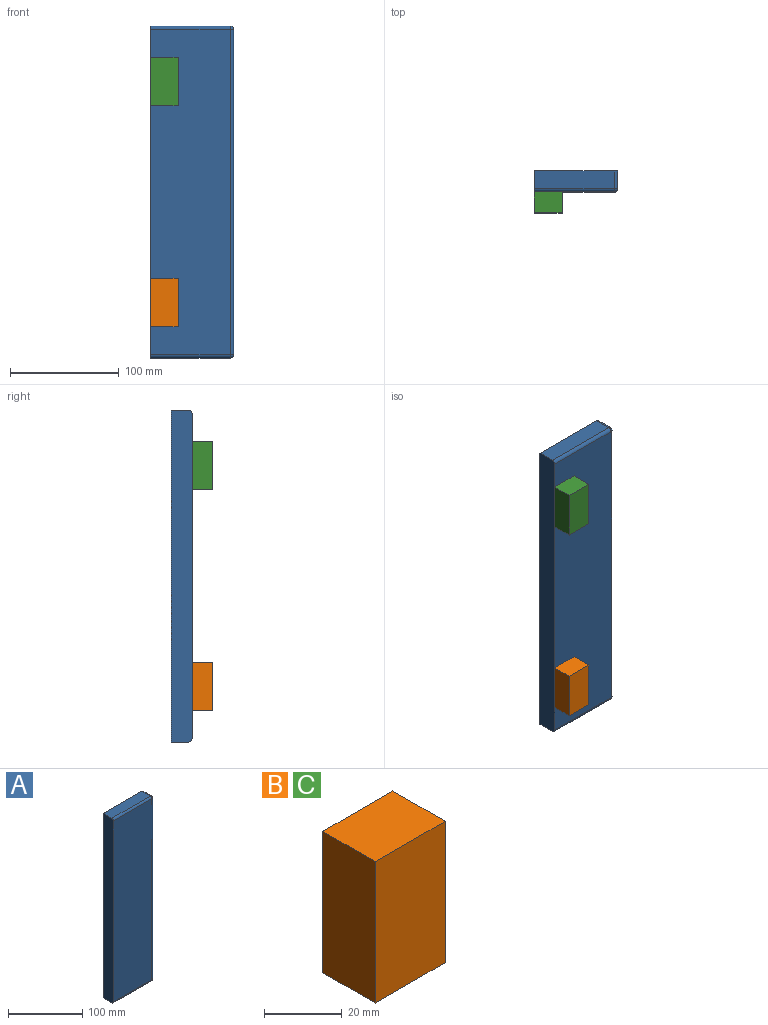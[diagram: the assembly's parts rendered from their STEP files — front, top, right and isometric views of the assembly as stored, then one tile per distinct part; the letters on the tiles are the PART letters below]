
ASSEMBLY  parts=3 mates=2
PART A: 13 faces, bbox 76.2x19.1x304.8 mm
  f0: plane 304.8x19.05mm, normal (-1,0,0), area 5802.6mm2, adj f1,f3,f4,f5,f6,f9
  f1: plane 73.2x16.05mm, normal (0,0,-1), area 1174.9mm2, adj f0,f5,f9,f12
  f2: plane 298.8x16.05mm, normal (1,0,0), area 4795.7mm2, adj f5,f7,f10,f12
  f3: plane 73.2x16.05mm, normal (0,0,1), area 1174.9mm2, adj f0,f5,f6,f7
  f4: plane 298.8x73.2mm, normal (0,-1,0), area 21872.2mm2, adj f0,f6,f9,f10
  f5: plane 304.8x76.2mm, normal (0,1,0), area 23221.9mm2, adj f0,f1,f2,f3,f7,f12
  f6: cylinder r=3mm len=73.2mm, axis (1,0,0), area 344.9mm2, adj f0,f3,f4,f8
  f7: cylinder r=3mm len=16.05mm, axis (0,-1,0), area 75.6mm2, adj f2,f3,f5,f8
  f8: sphere r=3mm, area 14.1mm2, adj f6,f7,f10
  f9: cylinder r=3mm len=73.2mm, axis (-1,0,0), area 344.9mm2, adj f0,f1,f4,f11
  f10: cylinder r=3mm len=298.8mm, axis (0,0,-1), area 1408.1mm2, adj f2,f4,f8,f11
  f11: sphere r=3mm, area 14.1mm2, adj f9,f10,f12
  f12: cylinder r=3mm len=16.05mm, axis (0,1,0), area 75.6mm2, adj f1,f2,f5,f11
PART B: 6 faces, bbox 25.4x19.1x44.5 mm
  f0: plane 44.45x19.05mm, normal (-1,0,0), area 846.8mm2, adj f1,f3,f4,f5
  f1: plane 25.4x19.05mm, normal (0,0,-1), area 483.9mm2, adj f0,f2,f4,f5
  f2: plane 44.45x19.05mm, normal (1,0,0), area 846.8mm2, adj f1,f3,f4,f5
  f3: plane 25.4x19.05mm, normal (0,0,1), area 483.9mm2, adj f0,f2,f4,f5
  f4: plane 44.45x25.4mm, normal (0,-1,0), area 1129mm2, adj f0,f1,f2,f3
  f5: plane 44.45x25.4mm, normal (0,1,0), area 1129mm2, adj f0,f1,f2,f3
PART C: same geometry as B
PLACE A at identity
PLACE B t=(-0.1,-19.05,28.57)mm
PLACE C t=(-0.1,-19.05,231.78)mm
MATE fastened C.f5 <-> A.f4  axis (0,1,0) through (12.6,-19.05,254)mm
MATE fastened B.f5 <-> A.f4  axis (0,1,0) through (12.6,-19.05,50.8)mm
